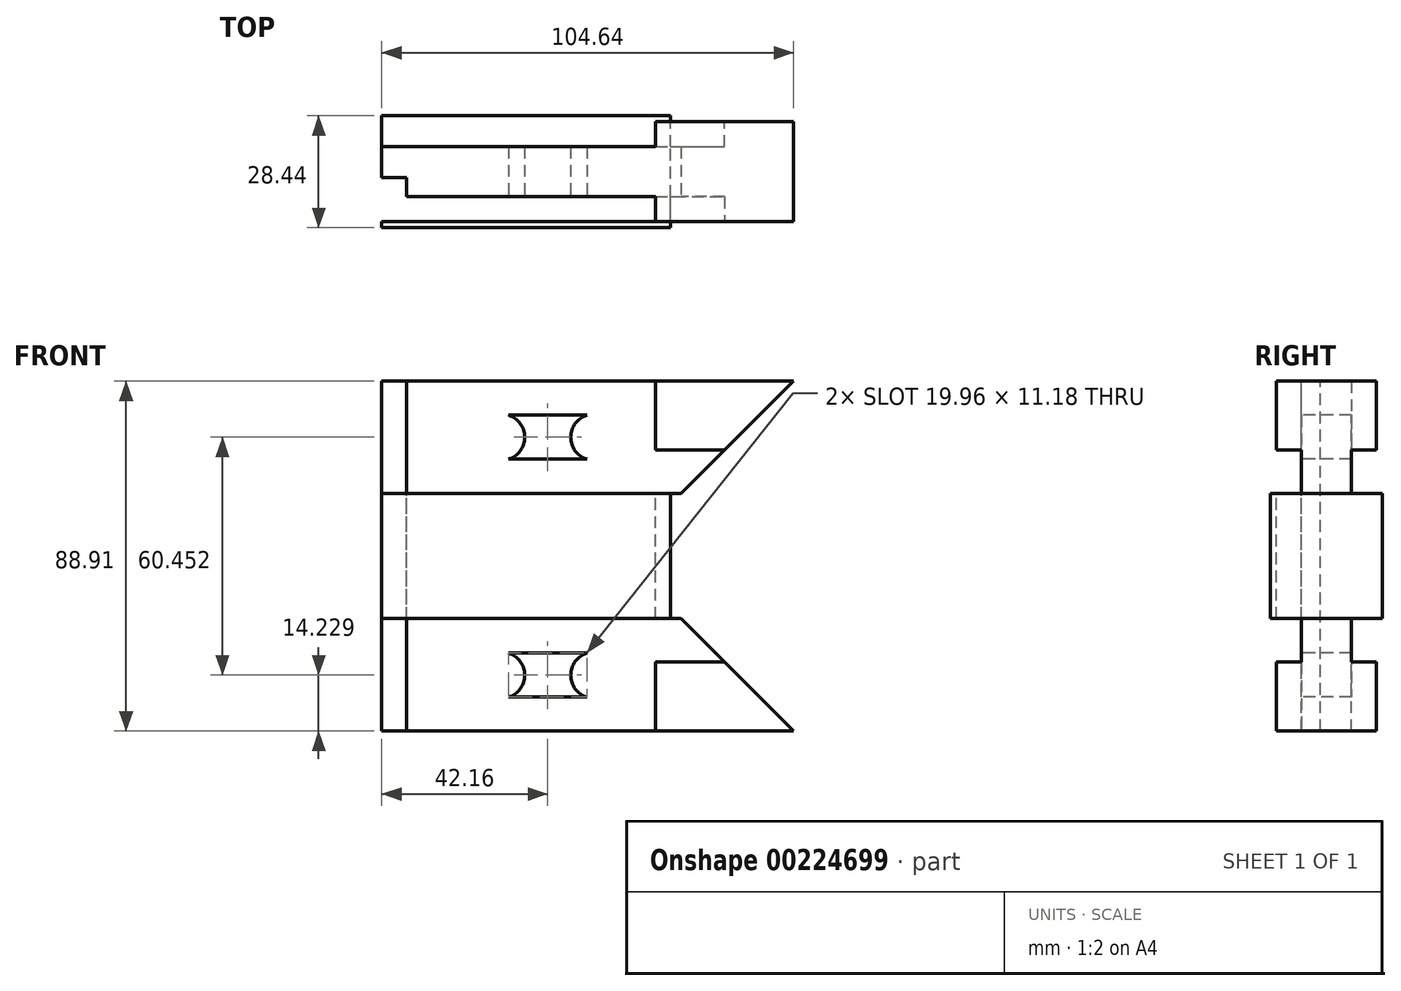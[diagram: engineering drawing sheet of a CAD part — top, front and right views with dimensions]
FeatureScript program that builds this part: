
annotation { "Feature Type Name" : "Feature", "Feature Type Description" : "" }
export const myFeature = defineFeature(function(context is Context, id is Id, definition is map)
    precondition{}
    {
        {
            var Q0;
            Q0=qCreatedBy(makeId("Top.planeOp"),FACE);
            var sketch = newSketch(context, id + "F0", { "sketchPlane" : qUnion([Q0])});
            skLineSegment(sketch, "E0.bottom", {"start": v(-52.32, -12.7) * mm, "end": v(52.32, -12.7) * mm});
            skLineSegment(sketch, "E0.top", {"start": v(-52.32, 12.7) * mm, "end": v(52.32, 12.7) * mm});
            skLineSegment(sketch, "E0.left", {"start": v(-52.32, -12.7) * mm, "end": v(-52.32, 12.7) * mm});
            skLineSegment(sketch, "E0.right", {"start": v(52.32, -12.7) * mm, "end": v(52.32, 12.7) * mm});
            skPoint(sketch, "E0.middle", {"position": v(0, 0) * mm});
            skLineSegment(sketch, "E1", {"start": v(-52.32, -12.7) * mm, "end": v(-52.32, -1.52) * mm});
            skLineSegment(sketch, "E2", {"start": v(-52.32, -1.52) * mm, "end": v(-45.97, -1.52) * mm});
            skLineSegment(sketch, "E3", {"start": v(-45.97, -1.52) * mm, "end": v(-45.97, -6.35) * mm});
            skLineSegment(sketch, "E4", {"start": v(-45.97, -6.35) * mm, "end": v(17.27, -6.35) * mm});
            skLineSegment(sketch, "E5", {"start": v(17.27, -6.35) * mm, "end": v(17.27, -12.7) * mm});
            skLineSegment(sketch, "E6", {"start": v(-52.32, 6.35) * mm, "end": v(17.27, 6.35) * mm});
            skLineSegment(sketch, "E7", {"start": v(17.27, 6.35) * mm, "end": v(17.27, 12.7) * mm});
            skLineSegment(sketch, "E8", {"start": v(-52.32, 0) * mm, "end": v(21.08, 0) * mm});
            skPoint(sketch, "E8.endSnap0", {"position": v(-52.32, 0) * mm});
            skLineSegment(sketch, "E9", {"start": v(21.08, 0) * mm, "end": v(21.08, 14.22) * mm});
            skLineSegment(sketch, "E10", {"start": v(21.08, 0) * mm, "end": v(21.08, -14.22) * mm});
            skLineSegment(sketch, "E11", {"start": v(21.08, 14.22) * mm, "end": v(-52.32, 14.22) * mm});
            skLineSegment(sketch, "E12", {"start": v(21.08, -14.22) * mm, "end": v(-52.32, -14.22) * mm});
            skLineSegment(sketch, "E13", {"start": v(-52.32, 14.22) * mm, "end": v(-52.32, 12.7) * mm});
            skLineSegment(sketch, "E14", {"start": v(-52.32, -14.22) * mm, "end": v(-52.32, -12.7) * mm});
            skSolve(sketch);
        }
        {
            var Q0;
            {var subQ1=sQuery(id+"F0.wireOp",EDGE,"E6");Q0=makeQuery(id+"F0.imprint","IMPRINT",FACE,{"disambiguationData":[TD([[makeQuery(id+"F0.imprint","IMPRINT",EDGE,{"derivedFrom":subQ1}),-1.0]])]});}
            var Q1;
            {var subQ4=sQuery(id+"F0.wireOp",EDGE,"E6");Q1=makeQuery(id+"F0.imprint","IMPRINT",FACE,{"disambiguationData":[TD([[makeQuery(id+"F0.imprint","IMPRINT",EDGE,{"derivedFrom":subQ4}),1.0]])]});}
            var Q2;
            {var subQ0=sQuery(id+"F0.wireOp",EDGE,"E1");Q2=makeQuery(id+"F0.imprint","IMPRINT",FACE,{"disambiguationData":[TD([[makeQuery(id+"F0.imprint","IMPRINT",EDGE,{"derivedFrom":subQ0}),-1.0]])]});}
            var Q3;
            {var subQ0=sQuery(id+"F0.wireOp",EDGE,"E2");Q3=makeQuery(id+"F0.imprint","IMPRINT",FACE,{"disambiguationData":[TD([[makeQuery(id+"F0.imprint","IMPRINT",EDGE,{"derivedFrom":subQ0}),1.0]])]});}
            var Q4;
            {var subQ0=sQuery(id+"F0.wireOp",EDGE,"E12");Q4=makeQuery(id+"F0.imprint","IMPRINT",FACE,{"disambiguationData":[TD([[makeQuery(id+"F0.imprint","IMPRINT",EDGE,{"derivedFrom":subQ0}),-1.0]])]});}
            var Q5;
            {var subQ0=sQuery(id+"F0.wireOp",EDGE,"E11");Q5=makeQuery(id+"F0.imprint","IMPRINT",FACE,{"disambiguationData":[TD([[makeQuery(id+"F0.imprint","IMPRINT",EDGE,{"derivedFrom":subQ0}),1.0]])]});}
            extrude(context, id + "F1", {"entities" : qUnion([Q0, Q1, Q2, Q3, Q4, Q5]), "oppositeDirection" : true, "depth" : 15.88 * mm});
        }
        {
            var Q0;
            {var subQ1=sQuery(id+"F0.wireOp",EDGE,"E6");Q0=makeQuery(id+"F0.imprint","IMPRINT",FACE,{"disambiguationData":[TD([[makeQuery(id+"F0.imprint","IMPRINT",EDGE,{"derivedFrom":subQ1}),-1.0]])]});}
            var Q1;
            {var subQ0=sQuery(id+"F0.wireOp",EDGE,"E0.right");Q1=makeQuery(id+"F0.imprint","IMPRINT",FACE,{"disambiguationData":[TD([[makeQuery(id+"F0.imprint","IMPRINT",EDGE,{"derivedFrom":subQ0}),1.0]])]});}
            var Q2;
            {var subQ0=sQuery(id+"F0.wireOp",EDGE,"E2");Q2=makeQuery(id+"F0.imprint","IMPRINT",FACE,{"disambiguationData":[TD([[makeQuery(id+"F0.imprint","IMPRINT",EDGE,{"derivedFrom":subQ0}),1.0]])]});}
            extrude(context, id + "F2", {"entities" : qUnion([Q0, Q1, Q2]), "operationType" : NewBodyOperationType.ADD, "depth" : 28.57 * mm});
        }
        {
            var Q0;
            Q0=makeQuery(id+"F2.opExtrude","SWEPT_FACE",FACE,{"disambiguationData":[OSD([sQuery(id+"F0.wireOp",EDGE,"E0.bottom")])]});
            var sketch = newSketch(context, id + "F3", { "sketchPlane" : qUnion([Q0])});
            skLineSegment(sketch, "E15", {"start": v(52.32, 28.58) * mm, "end": v(22.77, -0.98) * mm});
            skSolve(sketch);
        }
        {
            var Q0;
            {var subQ1=sQuery(id+"F0.wireOp",EDGE,"E0.bottom");var subQ2=sQuery(id+"F0.wireOp",EDGE,"E0.right");var subQ3=makeQuery(id+"F2.opExtrude","SWEPT_EDGE",EDGE,{"disambiguationData":[OSD([subQ1,subQ2])]});Q0=makeQuery(id+"F3.imprint","IMPRINT",FACE,{"disambiguationData":[TD([[makeQuery(id+"F3.imprint","IMPRINT",EDGE,{"derivedFrom":subQ3}),-1.0]])]});}
            extrude(context, id + "F4", {"entities" : qUnion([Q0]), "operationType" : NewBodyOperationType.REMOVE, "endBound" : BoundingType.THROUGH_ALL, "oppositeDirection" : true, "depth" : 25.4 * mm});
        }
        {
            var Q0;
            Q0=makeQuery(id+"F2.opExtrude","SWEPT_FACE",FACE,{"disambiguationData":[OSD([sQuery(id+"F0.wireOp",EDGE,"E0.bottom")])]});
            var sketch = newSketch(context, id + "F5", { "sketchPlane" : qUnion([Q0])});
            skLineSegment(sketch, "E16", {"start": v(17.27, 28.58) * mm, "end": v(17.27, 11.05) * mm});
            skLineSegment(sketch, "E17", {"start": v(17.27, 11.05) * mm, "end": v(34.8, 11.05) * mm});
            skSolve(sketch);
        }
        {
            var Q0;
            {var subQ14=sQuery(id+"F5.wireOp",EDGE,"E17");Q0=makeQuery(id+"F5.imprint","IMPRINT",FACE,{"disambiguationData":[TD([[makeQuery(id+"F5.imprint","IMPRINT",EDGE,{"derivedFrom":subQ14}),-1.0]])]});}
            extrude(context, id + "F6", {"entities" : qUnion([Q0]), "operationType" : NewBodyOperationType.REMOVE, "oppositeDirection" : true, "depth" : 6.35 * mm});
        }
        {
            var Q0;
            Q0=makeQuery(id+"F2.opExtrude","SWEPT_FACE",FACE,{"disambiguationData":[OSD([sQuery(id+"F0.wireOp",EDGE,"E0.top")])]});
            var sketch = newSketch(context, id + "F7", { "sketchPlane" : qUnion([Q0])});
            skLineSegment(sketch, "E18", {"start": v(-17.27, 28.58) * mm, "end": v(-17.27, 11.05) * mm});
            skLineSegment(sketch, "E19", {"start": v(-17.27, 11.05) * mm, "end": v(-34.8, 11.05) * mm});
            skSolve(sketch);
        }
        {
            var Q0;
            {var subQ14=sQuery(id+"F7.wireOp",EDGE,"E19");Q0=makeQuery(id+"F7.imprint","IMPRINT",FACE,{"disambiguationData":[TD([[makeQuery(id+"F7.imprint","IMPRINT",EDGE,{"derivedFrom":subQ14}),1.0]])]});}
            extrude(context, id + "F8", {"entities" : qUnion([Q0]), "operationType" : NewBodyOperationType.REMOVE, "oppositeDirection" : true, "depth" : 6.35 * mm});
        }
        {
            var Q0;
            Q0=makeQuery(id+"F6.boolean.opBoolean","MERGE",FACE,{"derivedFrom":[makeQuery(id+"F2.opExtrude","SWEPT_FACE",FACE,{"disambiguationData":[OSD([sQuery(id+"F0.wireOp",EDGE,"E4")])]}),makeQuery(id+"F6.opExtrude","CAP_FACE",FACE,{"disambiguationData":[OSD([sQuery(id+"F0.wireOp",EDGE,"E0.bottom"),sQuery(id+"F0.wireOp",EDGE,"E5"),sQuery(id+"F3.wireOp",EDGE,"E15"),sQuery(id+"F5.wireOp",EDGE,"E17")])],"isStart":false})]});
            var sketch = newSketch(context, id + "F9", { "sketchPlane" : qUnion([Q0])});
            skLineSegment(sketch, "E20", {"start": v(-45.97, 28.58) * mm, "end": v(-45.97, 14.35) * mm});
            skLineSegment(sketch, "E21", {"start": v(-45.97, 14.35) * mm, "end": v(-27.69, 14.35) * mm});
            skLineSegment(sketch, "E22", {"start": v(-27.69, 14.35) * mm, "end": v(7.37, 14.35) * mm});
            skLineSegment(sketch, "E23.bottom", {"start": v(7.37, 19.94) * mm, "end": v(-27.69, 19.94) * mm});
            skLineSegment(sketch, "E23.top", {"start": v(7.37, 8.76) * mm, "end": v(-27.69, 8.76) * mm});
            skLineSegment(sketch, "E23.left", {"start": v(7.37, 19.94) * mm, "end": v(7.37, 8.76) * mm});
            skLineSegment(sketch, "E23.right", {"start": v(-27.69, 19.94) * mm, "end": v(-27.69, 8.76) * mm});
            skPoint(sketch, "E23.middle", {"position": v(-10.16, 14.35) * mm});
            skLineSegment(sketch, "E24", {"start": v(-27.69, 14.35) * mm, "end": v(-21.84, 14.35) * mm});
            skLineSegment(sketch, "E25", {"start": v(7.37, 14.35) * mm, "end": v(1.52, 14.35) * mm});
            skArc(sketch, "E26", {"start": v(-23.55, 19.94) * mm, "mid": v(-27.69, 14.35) * mm, "end": v(-23.55, 8.76) * mm});
            skArc(sketch, "E27", {"start": v(-0.18, 19.94) * mm, "mid": v(-4.32, 14.35) * mm, "end": v(-0.18, 8.76) * mm});
            skArc(sketch, "E28.trimOffspring", {"start": v(-20.14, 8.76) * mm, "mid": v(-16, 14.35) * mm, "end": v(-20.14, 19.94) * mm});
            skArc(sketch, "E29.trimOffspring", {"start": v(3.23, 8.76) * mm, "mid": v(7.37, 14.35) * mm, "end": v(3.23, 19.94) * mm});
            skSolve(sketch);
        }
        {
            var Q0;
            {var subQ0=sQuery(id+"F9.wireOp",EDGE,"E24");Q0=makeQuery(id+"F9.imprint","IMPRINT",FACE,{"disambiguationData":[TD([[makeQuery(id+"F9.imprint","IMPRINT",EDGE,{"derivedFrom":subQ0}),1.0]])]});}
            var Q1;
            {var subQ1=sQuery(id+"F9.wireOp",EDGE,"E24");Q1=makeQuery(id+"F9.imprint","IMPRINT",FACE,{"disambiguationData":[TD([[makeQuery(id+"F9.imprint","IMPRINT",EDGE,{"derivedFrom":subQ1}),-1.0]])]});}
            var Q2;
            {var subQ0=sQuery(id+"F9.wireOp",EDGE,"E28.trimOffspring");var subQ1=sQuery(id+"F9.wireOp",EDGE,"E22");var subQ2=makeQuery(id+"F9.imprint","INTERSECT",VERTEX,{"derivedFrom":[subQ1,subQ0]});Q2=makeQuery(id+"F9.imprint","IMPRINT",FACE,{"disambiguationData":[TD([[makeQuery(id+"F9.imprint","IMPRINT",EDGE,{"disambiguationData":[TD([[subQ2,-1.0]])],"derivedFrom":subQ1}),1.0]])]});}
            var Q3;
            {var subQ0=sQuery(id+"F9.wireOp",EDGE,"E28.trimOffspring");var subQ1=sQuery(id+"F9.wireOp",EDGE,"E22");var subQ2=makeQuery(id+"F9.imprint","INTERSECT",VERTEX,{"derivedFrom":[subQ1,subQ0]});Q3=makeQuery(id+"F9.imprint","IMPRINT",FACE,{"disambiguationData":[TD([[makeQuery(id+"F9.imprint","IMPRINT",EDGE,{"disambiguationData":[TD([[subQ2,-1.0]])],"derivedFrom":subQ1}),-1.0]])]});}
            var Q4;
            {var subQ0=sQuery(id+"F9.wireOp",EDGE,"E25");Q4=makeQuery(id+"F9.imprint","IMPRINT",FACE,{"disambiguationData":[TD([[makeQuery(id+"F9.imprint","IMPRINT",EDGE,{"derivedFrom":subQ0}),-1.0]])]});}
            var Q5;
            {var subQ5=sQuery(id+"F9.wireOp",EDGE,"E25");Q5=makeQuery(id+"F9.imprint","IMPRINT",FACE,{"disambiguationData":[TD([[makeQuery(id+"F9.imprint","IMPRINT",EDGE,{"derivedFrom":subQ5}),1.0]])]});}
            extrude(context, id + "F10", {"entities" : qUnion([Q0, Q1, Q2, Q3, Q4, Q5]), "operationType" : NewBodyOperationType.REMOVE, "oppositeDirection" : true, "depth" : 50.8 * mm});
        }
        {
            var Q0;
            Q0=makeQuery(id+"F1.opExtrude","SWEPT_BODY",BODY,{"disambiguationData":[OSD([sQuery(id+"F0.wireOp",EDGE,"E0.left"),sQuery(id+"F0.wireOp",EDGE,"E1"),sQuery(id+"F0.wireOp",EDGE,"E9"),sQuery(id+"F0.wireOp",EDGE,"E10"),sQuery(id+"F0.wireOp",EDGE,"E11"),sQuery(id+"F0.wireOp",EDGE,"E12"),sQuery(id+"F0.wireOp",EDGE,"E13"),sQuery(id+"F0.wireOp",EDGE,"E14")])]});
            var Q1;
            Q1=makeQuery(id+"F1.opExtrude","CAP_FACE",FACE,{"disambiguationData":[OSD([sQuery(id+"F0.wireOp",EDGE,"E0.left"),sQuery(id+"F0.wireOp",EDGE,"E1"),sQuery(id+"F0.wireOp",EDGE,"E9"),sQuery(id+"F0.wireOp",EDGE,"E10"),sQuery(id+"F0.wireOp",EDGE,"E11"),sQuery(id+"F0.wireOp",EDGE,"E12"),sQuery(id+"F0.wireOp",EDGE,"E13"),sQuery(id+"F0.wireOp",EDGE,"E14")])],"isStart":false});
            mirror(context, id + "F11", {"operationType" : NewBodyOperationType.ADD, "entities" : qUnion([Q0]), "mirrorPlane" : qUnion([Q1])});
        }
    });
